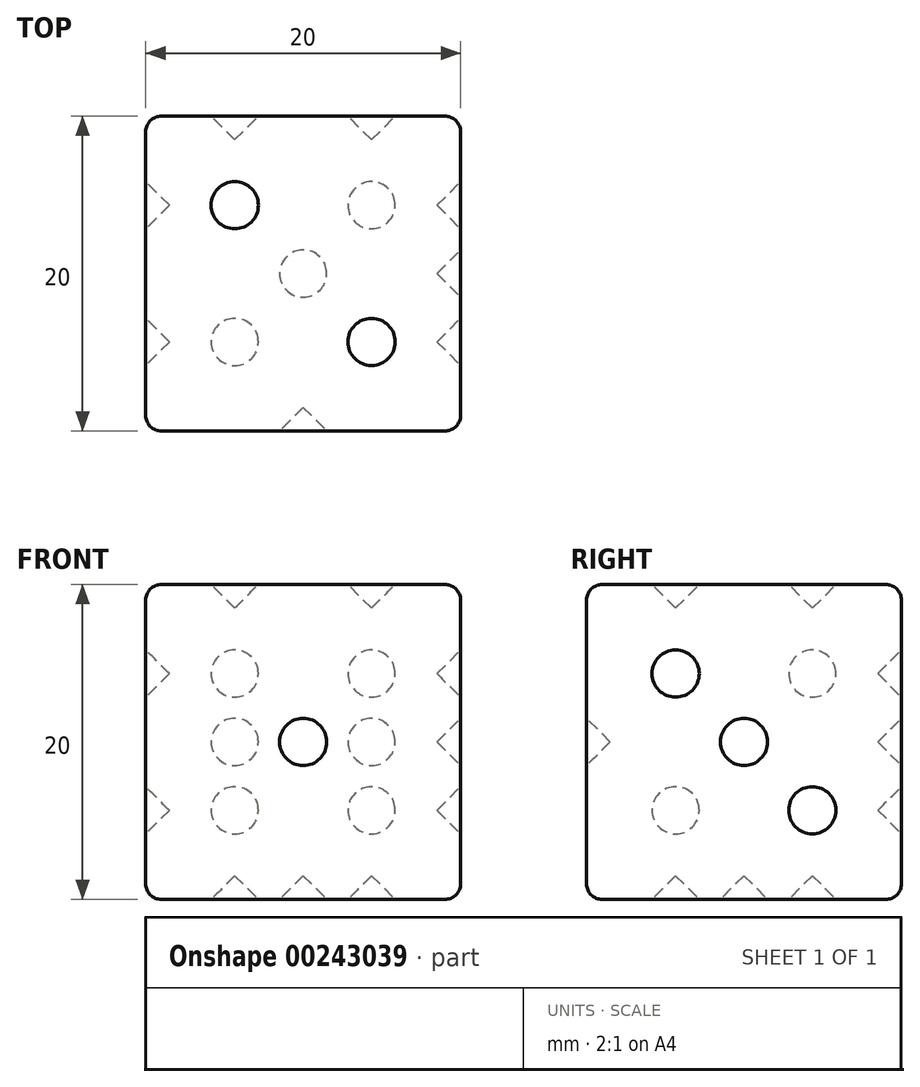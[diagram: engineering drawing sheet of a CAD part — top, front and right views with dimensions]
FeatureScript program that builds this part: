
annotation { "Feature Type Name" : "Feature", "Feature Type Description" : "" }
export const myFeature = defineFeature(function(context is Context, id is Id, definition is map)
    precondition{}
    {
        {
            var Q0;
            Q0=qCreatedBy(makeId("Top.planeOp"),FACE);
            var sketch = newSketch(context, id + "F0", { "sketchPlane" : qUnion([Q0])});
            skLineSegment(sketch, "E0.bottom", {"start": v(0, 0) * mm, "end": v(20, 0) * mm});
            skLineSegment(sketch, "E0.top", {"start": v(0, 20) * mm, "end": v(20, 20) * mm});
            skLineSegment(sketch, "E0.left", {"start": v(0, 0) * mm, "end": v(0, 20) * mm});
            skLineSegment(sketch, "E0.right", {"start": v(20, 0) * mm, "end": v(20, 20) * mm});
            skSolve(sketch);
        }
        {
            var Q0;
            Q0 = qSketchRegion(id + "F0", true);
            extrude(context, id + "F1", {"entities" : qUnion([Q0]), "depth" : 20 * mm});
        }
        {
            var Q0;
            Q0=makeQuery(id+"F1.opExtrude","SWEPT_FACE",FACE,{"disambiguationData":[OSD([sQuery(id+"F0.wireOp",EDGE,"E0.bottom")])]});
            var sketch = newSketch(context, id + "F2", { "sketchPlane" : qUnion([Q0])});
            skLineSegment(sketch, "E1", {"start": v(10, 20) * mm, "end": v(10, 0) * mm, "construction": true});
            skCircle(sketch, "E2", {"center": v(10, 10) * mm, "radius": 1.5 * mm});
            skSolve(sketch);
        }
        {
            var Q0;
            Q0 = qSketchRegion(id + "F2", true);
            extrude(context, id + "F3", {"entities" : qUnion([Q0]), "operationType" : NewBodyOperationType.REMOVE, "oppositeDirection" : true, "depth" : 1.5 * mm});
        }
        {
            var Q0;
            Q0=makeQuery(id+"F1.opExtrude","CAP_FACE",FACE,{"disambiguationData":[OSD([sQuery(id+"F0.wireOp",EDGE,"E0.bottom"),sQuery(id+"F0.wireOp",EDGE,"E0.top"),sQuery(id+"F0.wireOp",EDGE,"E0.left"),sQuery(id+"F0.wireOp",EDGE,"E0.right")])],"isStart":false});
            var sketch = newSketch(context, id + "F4", { "sketchPlane" : qUnion([Q0])});
            skLineSegment(sketch, "E3", {"start": v(0, 20) * mm, "end": v(5.66, 14.34) * mm, "construction": true});
            skLineSegment(sketch, "E4", {"start": v(20, 0) * mm, "end": v(14.34, 5.66) * mm, "construction": true});
            skCircle(sketch, "E5", {"center": v(5.66, 14.34) * mm, "radius": 1.5 * mm});
            skCircle(sketch, "E6", {"center": v(14.34, 5.66) * mm, "radius": 1.5 * mm});
            skSolve(sketch);
        }
        {
            var Q0;
            Q0=makeQuery(id+"F4.imprint","IMPRINT",FACE,{"disambiguationData":[TD([[makeQuery(id+"F4.imprint","IMPRINT",EDGE,{"derivedFrom":sQuery(id+"F4.wireOp",EDGE,"E6")}),1.0]])]});
            var Q1;
            Q1=makeQuery(id+"F4.imprint","IMPRINT",FACE,{"disambiguationData":[TD([[makeQuery(id+"F4.imprint","IMPRINT",EDGE,{"derivedFrom":sQuery(id+"F4.wireOp",EDGE,"E5")}),1.0]])]});
            var Q2;
            Q2=sQuery(id+"F4.wireOp",EDGE,"E5");
            var Q3;
            Q3=sQuery(id+"F4.wireOp",EDGE,"E6");
            extrude(context, id + "F5", {"entities" : qUnion([Q0, Q1]), "operationType" : NewBodyOperationType.REMOVE, "surfaceEntities" : qUnion([Q2, Q3]), "oppositeDirection" : true, "depth" : 1.5 * mm});
        }
        {
            var Q0;
            Q0=makeQuery(id+"F1.opExtrude","SWEPT_FACE",FACE,{"disambiguationData":[OSD([sQuery(id+"F0.wireOp",EDGE,"E0.right")])]});
            var sketch = newSketch(context, id + "F6", { "sketchPlane" : qUnion([Q0])});
            skLineSegment(sketch, "E7", {"start": v(20, 0) * mm, "end": v(14.34, 5.66) * mm, "construction": true});
            skLineSegment(sketch, "E8", {"start": v(0, 20) * mm, "end": v(5.66, 14.34) * mm, "construction": true});
            skCircle(sketch, "E9", {"center": v(5.66, 14.34) * mm, "radius": 1.5 * mm});
            skCircle(sketch, "E10", {"center": v(14.34, 5.66) * mm, "radius": 1.5 * mm});
            skLineSegment(sketch, "E11", {"start": v(20, 20) * mm, "end": v(0, 0) * mm, "construction": true});
            skCircle(sketch, "E12", {"center": v(10, 10) * mm, "radius": 1.5 * mm});
            skSolve(sketch);
        }
        {
            var Q0;
            Q0=makeQuery(id+"F6.imprint","IMPRINT",FACE,{"disambiguationData":[TD([[makeQuery(id+"F6.imprint","IMPRINT",EDGE,{"derivedFrom":sQuery(id+"F6.wireOp",EDGE,"E9")}),1.0]])]});
            var Q1;
            Q1=makeQuery(id+"F6.imprint","IMPRINT",FACE,{"disambiguationData":[TD([[makeQuery(id+"F6.imprint","IMPRINT",EDGE,{"derivedFrom":sQuery(id+"F6.wireOp",EDGE,"E12")}),1.0]])]});
            var Q2;
            Q2=makeQuery(id+"F6.imprint","IMPRINT",FACE,{"disambiguationData":[TD([[makeQuery(id+"F6.imprint","IMPRINT",EDGE,{"derivedFrom":sQuery(id+"F6.wireOp",EDGE,"E10")}),1.0]])]});
            var Q3;
            Q3=sQuery(id+"F6.wireOp",EDGE,"E9");
            var Q4;
            Q4=sQuery(id+"F6.wireOp",EDGE,"E12");
            var Q5;
            Q5=sQuery(id+"F6.wireOp",EDGE,"E10");
            extrude(context, id + "F7", {"entities" : qUnion([Q0, Q1, Q2]), "operationType" : NewBodyOperationType.REMOVE, "surfaceEntities" : qUnion([Q3, Q4, Q5]), "oppositeDirection" : true, "depth" : 1.5 * mm});
        }
        {
            var Q0;
            Q0=makeQuery(id+"F1.opExtrude","SWEPT_FACE",FACE,{"disambiguationData":[OSD([sQuery(id+"F0.wireOp",EDGE,"E0.top")])]});
            var sketch = newSketch(context, id + "F8", { "sketchPlane" : qUnion([Q0])});
            skLineSegment(sketch, "E13", {"start": v(0, 0) * mm, "end": v(-5.66, 5.66) * mm, "construction": true});
            skLineSegment(sketch, "E14", {"start": v(-20, 20) * mm, "end": v(-14.34, 14.34) * mm, "construction": true});
            skLineSegment(sketch, "E15", {"start": v(-20, 0) * mm, "end": v(-14.34, 5.66) * mm, "construction": true});
            skLineSegment(sketch, "E16", {"start": v(0, 20) * mm, "end": v(-5.66, 14.34) * mm, "construction": true});
            skCircle(sketch, "E17", {"center": v(-14.34, 14.34) * mm, "radius": 1.5 * mm});
            skCircle(sketch, "E18", {"center": v(-5.66, 14.34) * mm, "radius": 1.5 * mm});
            skCircle(sketch, "E19", {"center": v(-14.34, 5.66) * mm, "radius": 1.5 * mm});
            skCircle(sketch, "E20", {"center": v(-5.66, 5.66) * mm, "radius": 1.5 * mm});
            skLineSegment(sketch, "E21", {"start": v(-14.34, 14.34) * mm, "end": v(-5.66, 14.34) * mm, "construction": true});
            skLineSegment(sketch, "E22", {"start": v(-5.66, 5.66) * mm, "end": v(-14.34, 5.66) * mm, "construction": true});
            skLineSegment(sketch, "E23", {"start": v(-14.34, 14.34) * mm, "end": v(-14.34, 5.66) * mm, "construction": true});
            skLineSegment(sketch, "E24", {"start": v(-5.66, 14.34) * mm, "end": v(-5.66, 5.66) * mm, "construction": true});
            skCircle(sketch, "E25", {"center": v(-14.34, 10) * mm, "radius": 1.5 * mm});
            skCircle(sketch, "E26", {"center": v(-5.66, 10) * mm, "radius": 1.5 * mm});
            skSolve(sketch);
        }
        {
            var Q0;
            Q0=makeQuery(id+"F8.imprint","IMPRINT",FACE,{"disambiguationData":[TD([[makeQuery(id+"F8.imprint","IMPRINT",EDGE,{"derivedFrom":sQuery(id+"F8.wireOp",EDGE,"E25")}),1.0]])]});
            var Q1;
            Q1=makeQuery(id+"F8.imprint","IMPRINT",FACE,{"disambiguationData":[TD([[makeQuery(id+"F8.imprint","IMPRINT",EDGE,{"derivedFrom":sQuery(id+"F8.wireOp",EDGE,"E20")}),1.0]])]});
            var Q2;
            Q2=makeQuery(id+"F8.imprint","IMPRINT",FACE,{"disambiguationData":[TD([[makeQuery(id+"F8.imprint","IMPRINT",EDGE,{"derivedFrom":sQuery(id+"F8.wireOp",EDGE,"E17")}),1.0]])]});
            var Q3;
            Q3=makeQuery(id+"F8.imprint","IMPRINT",FACE,{"disambiguationData":[TD([[makeQuery(id+"F8.imprint","IMPRINT",EDGE,{"derivedFrom":sQuery(id+"F8.wireOp",EDGE,"E19")}),1.0]])]});
            var Q4;
            Q4=makeQuery(id+"F8.imprint","IMPRINT",FACE,{"disambiguationData":[TD([[makeQuery(id+"F8.imprint","IMPRINT",EDGE,{"derivedFrom":sQuery(id+"F8.wireOp",EDGE,"E18")}),1.0]])]});
            var Q5;
            Q5=makeQuery(id+"F8.imprint","IMPRINT",FACE,{"disambiguationData":[TD([[makeQuery(id+"F8.imprint","IMPRINT",EDGE,{"derivedFrom":sQuery(id+"F8.wireOp",EDGE,"E26")}),1.0]])]});
            var Q6;
            Q6=sQuery(id+"F8.wireOp",EDGE,"E19");
            var Q7;
            Q7=sQuery(id+"F8.wireOp",EDGE,"E25");
            var Q8;
            Q8=sQuery(id+"F8.wireOp",EDGE,"E20");
            var Q9;
            Q9=sQuery(id+"F8.wireOp",EDGE,"E26");
            var Q10;
            Q10=sQuery(id+"F8.wireOp",EDGE,"E18");
            var Q11;
            Q11=sQuery(id+"F8.wireOp",EDGE,"E17");
            extrude(context, id + "F9", {"entities" : qUnion([Q0, Q1, Q2, Q3, Q4, Q5]), "operationType" : NewBodyOperationType.REMOVE, "surfaceEntities" : qUnion([Q6, Q7, Q8, Q9, Q10, Q11]), "oppositeDirection" : true, "depth" : 1.5 * mm});
        }
        {
            var Q0;
            Q0=makeQuery(id+"F1.opExtrude","SWEPT_FACE",FACE,{"disambiguationData":[OSD([sQuery(id+"F0.wireOp",EDGE,"E0.left")])]});
            var sketch = newSketch(context, id + "F10", { "sketchPlane" : qUnion([Q0])});
            skLineSegment(sketch, "E27", {"start": v(0, 0) * mm, "end": v(-5.66, 5.66) * mm, "construction": true});
            skLineSegment(sketch, "E28", {"start": v(-14.34, 14.34) * mm, "end": v(-20, 20) * mm, "construction": true});
            skLineSegment(sketch, "E29", {"start": v(0, 20) * mm, "end": v(-5.66, 14.34) * mm, "construction": true});
            skLineSegment(sketch, "E30", {"start": v(-20, 0) * mm, "end": v(-14.34, 5.66) * mm, "construction": true});
            skCircle(sketch, "E31", {"center": v(-14.34, 14.34) * mm, "radius": 1.5 * mm});
            skCircle(sketch, "E32", {"center": v(-14.34, 5.66) * mm, "radius": 1.5 * mm});
            skCircle(sketch, "E33", {"center": v(-5.66, 5.66) * mm, "radius": 1.5 * mm});
            skCircle(sketch, "E34", {"center": v(-5.66, 14.34) * mm, "radius": 1.5 * mm});
            skSolve(sketch);
        }
        {
            var Q0;
            Q0=makeQuery(id+"F10.imprint","IMPRINT",FACE,{"disambiguationData":[TD([[makeQuery(id+"F10.imprint","IMPRINT",EDGE,{"derivedFrom":sQuery(id+"F10.wireOp",EDGE,"E32")}),1.0]])]});
            var Q1;
            Q1=makeQuery(id+"F10.imprint","IMPRINT",FACE,{"disambiguationData":[TD([[makeQuery(id+"F10.imprint","IMPRINT",EDGE,{"derivedFrom":sQuery(id+"F10.wireOp",EDGE,"E33")}),1.0]])]});
            var Q2;
            Q2=makeQuery(id+"F10.imprint","IMPRINT",FACE,{"disambiguationData":[TD([[makeQuery(id+"F10.imprint","IMPRINT",EDGE,{"derivedFrom":sQuery(id+"F10.wireOp",EDGE,"E31")}),1.0]])]});
            var Q3;
            Q3=makeQuery(id+"F10.imprint","IMPRINT",FACE,{"disambiguationData":[TD([[makeQuery(id+"F10.imprint","IMPRINT",EDGE,{"derivedFrom":sQuery(id+"F10.wireOp",EDGE,"E34")}),1.0]])]});
            var Q4;
            Q4=sQuery(id+"F10.wireOp",EDGE,"E34");
            var Q5;
            Q5=sQuery(id+"F10.wireOp",EDGE,"E32");
            var Q6;
            Q6=sQuery(id+"F10.wireOp",EDGE,"E33");
            var Q7;
            Q7=sQuery(id+"F10.wireOp",EDGE,"E31");
            extrude(context, id + "F11", {"entities" : qUnion([Q0, Q1, Q2, Q3]), "operationType" : NewBodyOperationType.REMOVE, "surfaceEntities" : qUnion([Q4, Q5, Q6, Q7]), "oppositeDirection" : true, "depth" : 1.5 * mm});
        }
        {
            var Q0;
            Q0=makeQuery(id+"F1.opExtrude","CAP_FACE",FACE,{"disambiguationData":[OSD([sQuery(id+"F0.wireOp",EDGE,"E0.bottom"),sQuery(id+"F0.wireOp",EDGE,"E0.top"),sQuery(id+"F0.wireOp",EDGE,"E0.left"),sQuery(id+"F0.wireOp",EDGE,"E0.right")])],"isStart":true});
            var sketch = newSketch(context, id + "F12", { "sketchPlane" : qUnion([Q0])});
            skLineSegment(sketch, "E35", {"start": v(20, -20) * mm, "end": v(14.34, -14.34) * mm, "construction": true});
            skLineSegment(sketch, "E36", {"start": v(5.66, -5.66) * mm, "end": v(0, 0) * mm, "construction": true});
            skLineSegment(sketch, "E37", {"start": v(20, 0) * mm, "end": v(14.34, -5.66) * mm, "construction": true});
            skLineSegment(sketch, "E38", {"start": v(5.66, -14.34) * mm, "end": v(0, -20) * mm, "construction": true});
            skCircle(sketch, "E39", {"center": v(5.66, -5.66) * mm, "radius": 1.5 * mm});
            skCircle(sketch, "E40", {"center": v(5.66, -14.34) * mm, "radius": 1.5 * mm});
            skCircle(sketch, "E41", {"center": v(14.34, -14.34) * mm, "radius": 1.5 * mm});
            skCircle(sketch, "E42", {"center": v(14.34, -5.66) * mm, "radius": 1.5 * mm});
            skLineSegment(sketch, "E43", {"start": v(5.66, -14.34) * mm, "end": v(14.34, -5.66) * mm, "construction": true});
            skCircle(sketch, "E44", {"center": v(10, -10) * mm, "radius": 1.5 * mm});
            skSolve(sketch);
        }
        {
            var Q0;
            Q0=makeQuery(id+"F12.imprint","IMPRINT",FACE,{"disambiguationData":[TD([[makeQuery(id+"F12.imprint","IMPRINT",EDGE,{"derivedFrom":sQuery(id+"F12.wireOp",EDGE,"E41")}),1.0]])]});
            var Q1;
            Q1=makeQuery(id+"F12.imprint","IMPRINT",FACE,{"disambiguationData":[TD([[makeQuery(id+"F12.imprint","IMPRINT",EDGE,{"derivedFrom":sQuery(id+"F12.wireOp",EDGE,"E39")}),1.0]])]});
            var Q2;
            Q2=makeQuery(id+"F12.imprint","IMPRINT",FACE,{"disambiguationData":[TD([[makeQuery(id+"F12.imprint","IMPRINT",EDGE,{"derivedFrom":sQuery(id+"F12.wireOp",EDGE,"E40")}),1.0]])]});
            var Q3;
            Q3=makeQuery(id+"F12.imprint","IMPRINT",FACE,{"disambiguationData":[TD([[makeQuery(id+"F12.imprint","IMPRINT",EDGE,{"derivedFrom":sQuery(id+"F12.wireOp",EDGE,"E42")}),1.0]])]});
            var Q4;
            Q4=makeQuery(id+"F12.imprint","IMPRINT",FACE,{"disambiguationData":[TD([[makeQuery(id+"F12.imprint","IMPRINT",EDGE,{"derivedFrom":sQuery(id+"F12.wireOp",EDGE,"E44")}),1.0]])]});
            var Q5;
            Q5=sQuery(id+"F12.wireOp",EDGE,"E39");
            var Q6;
            Q6=sQuery(id+"F12.wireOp",EDGE,"E42");
            var Q7;
            Q7=sQuery(id+"F12.wireOp",EDGE,"E41");
            var Q8;
            Q8=sQuery(id+"F12.wireOp",EDGE,"E40");
            extrude(context, id + "F13", {"entities" : qUnion([Q0, Q1, Q2, Q3, Q4]), "operationType" : NewBodyOperationType.REMOVE, "surfaceEntities" : qUnion([Q5, Q6, Q7, Q8]), "oppositeDirection" : true, "depth" : 1.5 * mm});
        }
        {
            var Q0;
            Q0=makeQuery(id+"F1.opExtrude","CAP_EDGE",EDGE,{"disambiguationData":[OSD([sQuery(id+"F0.wireOp",EDGE,"E0.right")])],"isStart":false});
            var Q1;
            Q1=makeQuery(id+"F1.opExtrude","SWEPT_EDGE",EDGE,{"disambiguationData":[OSD([sQuery(id+"F0.wireOp",EDGE,"E0.bottom"),sQuery(id+"F0.wireOp",EDGE,"E0.right")])]});
            var Q2;
            Q2=makeQuery(id+"F1.opExtrude","CAP_EDGE",EDGE,{"disambiguationData":[OSD([sQuery(id+"F0.wireOp",EDGE,"E0.bottom")])],"isStart":false});
            var Q3;
            Q3=makeQuery(id+"F1.opExtrude","SWEPT_EDGE",EDGE,{"disambiguationData":[OSD([sQuery(id+"F0.wireOp",EDGE,"E0.top"),sQuery(id+"F0.wireOp",EDGE,"E0.right")])]});
            var Q4;
            Q4=makeQuery(id+"F1.opExtrude","CAP_EDGE",EDGE,{"disambiguationData":[OSD([sQuery(id+"F0.wireOp",EDGE,"E0.right")])],"isStart":true});
            var Q5;
            Q5=makeQuery(id+"F1.opExtrude","CAP_EDGE",EDGE,{"disambiguationData":[OSD([sQuery(id+"F0.wireOp",EDGE,"E0.top")])],"isStart":true});
            var Q6;
            Q6=makeQuery(id+"F1.opExtrude","SWEPT_EDGE",EDGE,{"disambiguationData":[OSD([sQuery(id+"F0.wireOp",EDGE,"E0.top"),sQuery(id+"F0.wireOp",EDGE,"E0.left")])]});
            var Q7;
            Q7=makeQuery(id+"F1.opExtrude","CAP_EDGE",EDGE,{"disambiguationData":[OSD([sQuery(id+"F0.wireOp",EDGE,"E0.left")])],"isStart":false});
            var Q8;
            Q8=makeQuery(id+"F1.opExtrude","CAP_EDGE",EDGE,{"disambiguationData":[OSD([sQuery(id+"F0.wireOp",EDGE,"E0.top")])],"isStart":false});
            var Q9;
            Q9=makeQuery(id+"F1.opExtrude","SWEPT_EDGE",EDGE,{"disambiguationData":[OSD([sQuery(id+"F0.wireOp",EDGE,"E0.bottom"),sQuery(id+"F0.wireOp",EDGE,"E0.left")])]});
            var Q10;
            Q10=makeQuery(id+"F1.opExtrude","CAP_EDGE",EDGE,{"disambiguationData":[OSD([sQuery(id+"F0.wireOp",EDGE,"E0.left")])],"isStart":true});
            var Q11;
            Q11=makeQuery(id+"F1.opExtrude","CAP_EDGE",EDGE,{"disambiguationData":[OSD([sQuery(id+"F0.wireOp",EDGE,"E0.bottom")])],"isStart":true});
            fillet(context, id + "F14", {"entities" : qUnion([Q0, Q1, Q2, Q3, Q4, Q5, Q6, Q7, Q8, Q9, Q10, Q11]), "radius" : 1 * mm, "tangentPropagation" : true, "allowEdgeOverflow" : false});
        }
        {
            var Q0;
            Q0=makeQuery(id+"F5.boolean.opBoolean","COPY",EDGE,{"derivedFrom":makeQuery(id+"F5.opExtrude","CAP_EDGE",EDGE,{"disambiguationData":[OSD([sQuery(id+"F4.wireOp",EDGE,"E6")])],"isStart":false})});
            var Q1;
            Q1=makeQuery(id+"F3.boolean.opBoolean","COPY",EDGE,{"derivedFrom":makeQuery(id+"F3.opExtrude","CAP_EDGE",EDGE,{"disambiguationData":[OSD([sQuery(id+"F2.wireOp",EDGE,"E2")])],"isStart":false})});
            var Q2;
            Q2=makeQuery(id+"F5.boolean.opBoolean","COPY",EDGE,{"derivedFrom":makeQuery(id+"F5.opExtrude","CAP_EDGE",EDGE,{"disambiguationData":[OSD([sQuery(id+"F4.wireOp",EDGE,"E5")])],"isStart":false})});
            var Q3;
            Q3=makeQuery(id+"F9.boolean.opBoolean","COPY",EDGE,{"derivedFrom":makeQuery(id+"F9.opExtrude","CAP_EDGE",EDGE,{"disambiguationData":[OSD([sQuery(id+"F8.wireOp",EDGE,"E17")])],"isStart":false})});
            var Q4;
            Q4=makeQuery(id+"F9.boolean.opBoolean","COPY",FACE,{"derivedFrom":makeQuery(id+"F9.opExtrude","CAP_FACE",FACE,{"disambiguationData":[OSD([sQuery(id+"F8.wireOp",EDGE,"E25")])],"isStart":false})});
            var Q5;
            Q5=makeQuery(id+"F9.boolean.opBoolean","COPY",EDGE,{"derivedFrom":makeQuery(id+"F9.opExtrude","CAP_EDGE",EDGE,{"disambiguationData":[OSD([sQuery(id+"F8.wireOp",EDGE,"E19")])],"isStart":false})});
            var Q6;
            Q6=makeQuery(id+"F9.boolean.opBoolean","COPY",FACE,{"derivedFrom":makeQuery(id+"F9.opExtrude","CAP_FACE",FACE,{"disambiguationData":[OSD([sQuery(id+"F8.wireOp",EDGE,"E20")])],"isStart":false})});
            var Q7;
            Q7=makeQuery(id+"F9.boolean.opBoolean","COPY",EDGE,{"derivedFrom":makeQuery(id+"F9.opExtrude","CAP_EDGE",EDGE,{"disambiguationData":[OSD([sQuery(id+"F8.wireOp",EDGE,"E26")])],"isStart":false})});
            var Q8;
            Q8=makeQuery(id+"F9.boolean.opBoolean","COPY",EDGE,{"derivedFrom":makeQuery(id+"F9.opExtrude","CAP_EDGE",EDGE,{"disambiguationData":[OSD([sQuery(id+"F8.wireOp",EDGE,"E18")])],"isStart":false})});
            var Q9;
            Q9=makeQuery(id+"F7.boolean.opBoolean","COPY",EDGE,{"derivedFrom":makeQuery(id+"F7.opExtrude","CAP_EDGE",EDGE,{"disambiguationData":[OSD([sQuery(id+"F6.wireOp",EDGE,"E9")])],"isStart":false})});
            var Q10;
            Q10=makeQuery(id+"F7.boolean.opBoolean","COPY",FACE,{"derivedFrom":makeQuery(id+"F7.opExtrude","CAP_FACE",FACE,{"disambiguationData":[OSD([sQuery(id+"F6.wireOp",EDGE,"E12")])],"isStart":false})});
            var Q11;
            Q11=makeQuery(id+"F7.boolean.opBoolean","COPY",EDGE,{"derivedFrom":makeQuery(id+"F7.opExtrude","CAP_EDGE",EDGE,{"disambiguationData":[OSD([sQuery(id+"F6.wireOp",EDGE,"E10")])],"isStart":false})});
            var Q12;
            Q12=makeQuery(id+"F11.boolean.opBoolean","COPY",EDGE,{"derivedFrom":makeQuery(id+"F11.opExtrude","CAP_EDGE",EDGE,{"disambiguationData":[OSD([sQuery(id+"F10.wireOp",EDGE,"E31")])],"isStart":false})});
            var Q13;
            Q13=makeQuery(id+"F11.boolean.opBoolean","COPY",EDGE,{"derivedFrom":makeQuery(id+"F11.opExtrude","CAP_EDGE",EDGE,{"disambiguationData":[OSD([sQuery(id+"F10.wireOp",EDGE,"E34")])],"isStart":false})});
            var Q14;
            Q14=makeQuery(id+"F11.boolean.opBoolean","COPY",EDGE,{"derivedFrom":makeQuery(id+"F11.opExtrude","CAP_EDGE",EDGE,{"disambiguationData":[OSD([sQuery(id+"F10.wireOp",EDGE,"E33")])],"isStart":false})});
            var Q15;
            Q15=makeQuery(id+"F11.boolean.opBoolean","COPY",EDGE,{"derivedFrom":makeQuery(id+"F11.opExtrude","CAP_EDGE",EDGE,{"disambiguationData":[OSD([sQuery(id+"F10.wireOp",EDGE,"E32")])],"isStart":false})});
            var Q16;
            Q16=makeQuery(id+"F13.boolean.opBoolean","COPY",EDGE,{"derivedFrom":makeQuery(id+"F13.opExtrude","CAP_EDGE",EDGE,{"disambiguationData":[OSD([sQuery(id+"F12.wireOp",EDGE,"E39")])],"isStart":false})});
            var Q17;
            Q17=makeQuery(id+"F13.boolean.opBoolean","COPY",EDGE,{"derivedFrom":makeQuery(id+"F13.opExtrude","CAP_EDGE",EDGE,{"disambiguationData":[OSD([sQuery(id+"F12.wireOp",EDGE,"E40")])],"isStart":false})});
            var Q18;
            Q18=makeQuery(id+"F13.boolean.opBoolean","COPY",EDGE,{"derivedFrom":makeQuery(id+"F13.opExtrude","CAP_EDGE",EDGE,{"disambiguationData":[OSD([sQuery(id+"F12.wireOp",EDGE,"E44")])],"isStart":false})});
            var Q19;
            Q19=makeQuery(id+"F13.boolean.opBoolean","COPY",EDGE,{"derivedFrom":makeQuery(id+"F13.opExtrude","CAP_EDGE",EDGE,{"disambiguationData":[OSD([sQuery(id+"F12.wireOp",EDGE,"E41")])],"isStart":false})});
            var Q20;
            Q20=makeQuery(id+"F13.boolean.opBoolean","COPY",EDGE,{"derivedFrom":makeQuery(id+"F13.opExtrude","CAP_EDGE",EDGE,{"disambiguationData":[OSD([sQuery(id+"F12.wireOp",EDGE,"E42")])],"isStart":false})});
            chamfer(context, id + "F15", {"entities" : qUnion([Q0, Q1, Q2, Q3, Q4, Q5, Q6, Q7, Q8, Q9, Q10, Q11, Q12, Q13, Q14, Q15, Q16, Q17, Q18, Q19, Q20]), "width" : 1.5 * mm, "tangentPropagation" : true});
        }
    });
